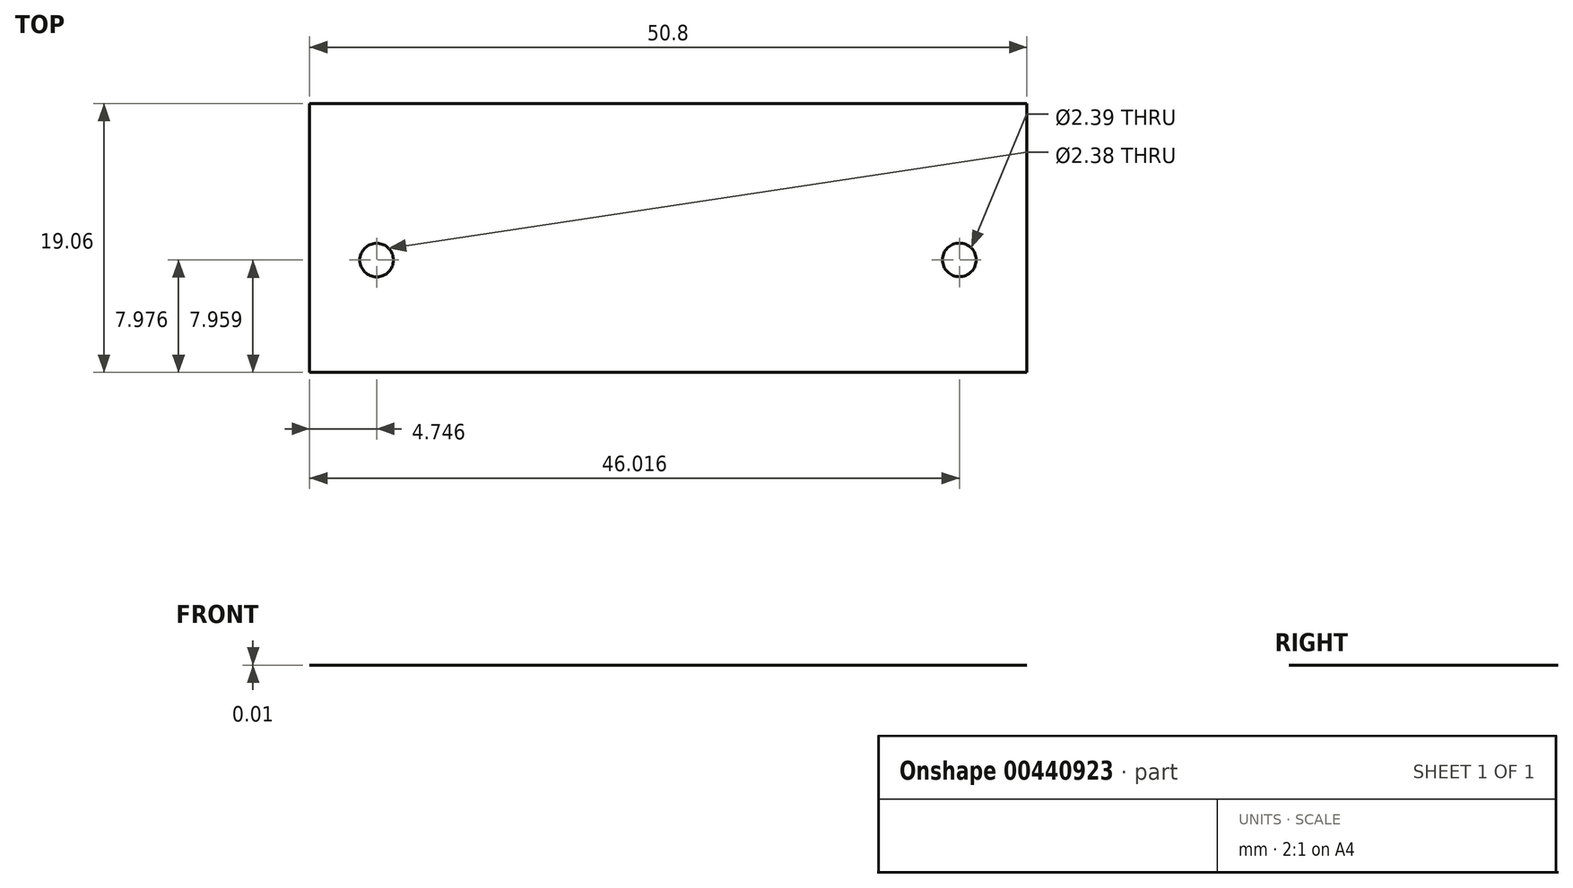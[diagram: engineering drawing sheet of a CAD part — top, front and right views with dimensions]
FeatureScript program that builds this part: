
annotation { "Feature Type Name" : "Feature", "Feature Type Description" : "" }
export const myFeature = defineFeature(function(context is Context, id is Id, definition is map)
    precondition{}
    {
        {
            var Q0;
            Q0=qCreatedBy(makeId("Top.planeOp"),FACE);
            var sketch = newSketch(context, id + "F0", { "sketchPlane" : qUnion([Q0])});
            skLineSegment(sketch, "E0.bottom", {"start": v(25.4, 9.53) * mm, "end": v(-25.4, 9.53) * mm});
            skLineSegment(sketch, "E0.top", {"start": v(25.4, -9.52) * mm, "end": v(-25.4, -9.52) * mm});
            skLineSegment(sketch, "E0.left", {"start": v(25.4, 9.53) * mm, "end": v(25.4, -9.52) * mm});
            skLineSegment(sketch, "E0.right", {"start": v(-25.4, 9.53) * mm, "end": v(-25.4, -9.52) * mm});
            skPoint(sketch, "E0.middle", {"position": v(0, 0) * mm});
            skSolve(sketch);
        }
        {
            var Q0;
            Q0=makeQuery(id+"F0.imprint","IMPRINT",FACE,{"disambiguationData":[TD([[makeQuery(id+"F0.imprint","IMPRINT",EDGE,{"derivedFrom":sQuery(id+"F0.wireOp",EDGE,"E0.bottom")}),1.0]])]});
            var sketch = newSketch(context, id + "F1", { "sketchPlane" : qUnion([Q0])});
            skCircle(sketch, "E1", {"center": v(-20.65, -1.57) * mm, "radius": 1.2 * mm});
            skSolve(sketch);
        }
        {
            var Q0;
            Q0=makeQuery(id+"F0.imprint","IMPRINT",FACE,{"disambiguationData":[TD([[makeQuery(id+"F0.imprint","IMPRINT",EDGE,{"derivedFrom":sQuery(id+"F0.wireOp",EDGE,"E0.bottom")}),1.0]])]});
            var sketch = newSketch(context, id + "F2", { "sketchPlane" : qUnion([Q0])});
            skCircle(sketch, "E2", {"center": v(20.62, -1.55) * mm, "radius": 1.2 * mm});
            skSolve(sketch);
        }
        {
            var Q0;
            Q0=makeQuery(id+"F0.imprint","IMPRINT",FACE,{"disambiguationData":[TD([[makeQuery(id+"F0.imprint","IMPRINT",EDGE,{"derivedFrom":sQuery(id+"F0.wireOp",EDGE,"E0.bottom")}),1.0]])]});
            extrude(context, id + "F3", {"entities" : qUnion([Q0]), "depth" : 6 / 812.8 * mm});
        }
        {
            var Q0;
            Q0 = qSketchRegion(id + "F2", true);
            extrude(context, id + "F4", {"entities" : qUnion([Q0]), "operationType" : NewBodyOperationType.REMOVE, "depth" : 6 / 812.8 * mm});
        }
        {
            var Q0;
            Q0 = qSketchRegion(id + "F1", true);
            extrude(context, id + "F5", {"entities" : qUnion([Q0]), "operationType" : NewBodyOperationType.REMOVE, "depth" : 6 / 812.8 * mm});
        }
    });
